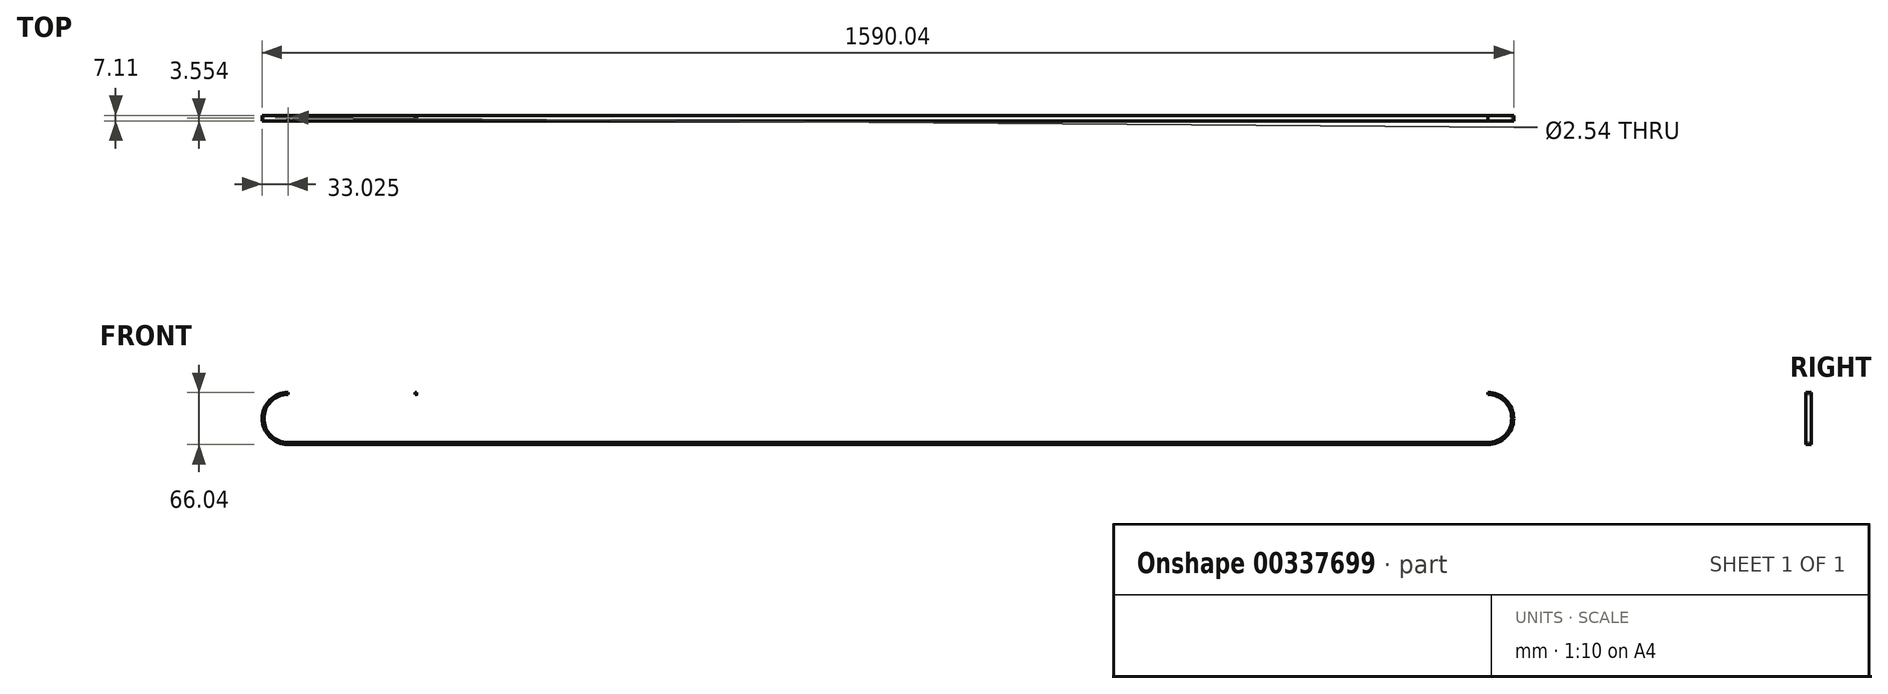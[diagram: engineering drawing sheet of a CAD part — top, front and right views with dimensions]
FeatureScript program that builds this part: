
annotation { "Feature Type Name" : "Feature", "Feature Type Description" : "" }
export const myFeature = defineFeature(function(context is Context, id is Id, definition is map)
    precondition{}
    {
        {
            var Q0;
            Q0=qCreatedBy(makeId("Front.planeOp"),FACE);
            var sketch = newSketch(context, id + "F0", { "sketchPlane" : qUnion([Q0])});
            skArc(sketch, "E0", {"start": v(1389.55, 13.92) * mm, "mid": v(1422.57, 46.94) * mm, "end": v(1389.55, 79.96) * mm});
            skArc(sketch, "E1", {"start": v(-134.45, 77.42) * mm, "mid": v(-164.93, 46.94) * mm, "end": v(-134.45, 16.46) * mm});
            skLineSegment(sketch, "E2", {"start": v(1389.55, 16.46) * mm, "end": v(-134.45, 16.46) * mm});
            skArc(sketch, "E3", {"start": v(-134.45, 79.96) * mm, "mid": v(-167.47, 46.94) * mm, "end": v(-134.45, 13.92) * mm});
            skLineSegment(sketch, "E4", {"start": v(-134.45, 13.92) * mm, "end": v(1389.55, 13.92) * mm});
            skLineSegment(sketch, "E5", {"start": v(-134.45, 79.96) * mm, "end": v(1389.55, 79.96) * mm});
            skLineSegment(sketch, "E6", {"start": v(-134.45, 77.42) * mm, "end": v(1389.55, 77.42) * mm});
            skArc(sketch, "E7", {"start": v(1389.55, 16.46) * mm, "mid": v(1420.03, 46.94) * mm, "end": v(1389.55, 77.42) * mm});
            skPoint(sketch, "E8", {"position": v(28.11, 79.96) * mm});
            skPoint(sketch, "E9", {"position": v(1330.37, 13.92) * mm});
            skSolve(sketch);
        }
        {
            var Q0;
            Q0 = qSketchRegion(id + "F0", true);
            extrude(context, id + "F1", {"entities" : qUnion([Q0]), "depth" : 7.11 * mm});
        }
        {
            var Q0;
            Q0=makeQuery(id+"F1.opExtrude","SWEPT_FACE",FACE,{"disambiguationData":[OSD([sQuery(id+"F0.wireOp",EDGE,"E5")])]});
            var sketch = newSketch(context, id + "F2", { "sketchPlane" : qUnion([Q0])});
            skLineSegment(sketch, "E10", {"start": v(28.11, 0) * mm, "end": v(28.11, -7.11) * mm});
            skPoint(sketch, "E11", {"position": v(28.11, -3.56) * mm});
            skCircle(sketch, "E12", {"center": v(28.11, -3.56) * mm, "radius": 1.08 * mm});
            skSolve(sketch);
        }
        {
            var Q0;
            {var subQ0=sQuery(id+"F2.wireOp",EDGE,"E12");var subQ1=sQuery(id+"F2.wireOp",EDGE,"E10");var subQ2=makeQuery(id+"F2.imprint","INTERSECT",VERTEX,{"disambiguationData":[OD(0.0)],"derivedFrom":[subQ1,subQ0]});Q0=makeQuery(id+"F2.imprint","IMPRINT",FACE,{"disambiguationData":[TD([[makeQuery(id+"F2.imprint","IMPRINT",EDGE,{"disambiguationData":[TD([[subQ2,-1.0]])],"derivedFrom":subQ1}),-1.0]])]});}
            var Q1;
            {var subQ0=sQuery(id+"F2.wireOp",EDGE,"E12");var subQ1=sQuery(id+"F2.wireOp",EDGE,"E10");var subQ2=makeQuery(id+"F2.imprint","INTERSECT",VERTEX,{"disambiguationData":[OD(0.0)],"derivedFrom":[subQ1,subQ0]});Q1=makeQuery(id+"F2.imprint","IMPRINT",FACE,{"disambiguationData":[TD([[makeQuery(id+"F2.imprint","IMPRINT",EDGE,{"disambiguationData":[TD([[subQ2,-1.0]])],"derivedFrom":subQ1}),1.0]])]});}
            extrude(context, id + "F3", {"entities" : qUnion([Q0, Q1]), "operationType" : NewBodyOperationType.REMOVE, "oppositeDirection" : true, "depth" : 25.4 * mm});
        }
        {
            var Q0;
            Q0=makeQuery(id+"F1.opExtrude","SWEPT_FACE",FACE,{"disambiguationData":[OSD([sQuery(id+"F0.wireOp",EDGE,"E4")])]});
            var sketch = newSketch(context, id + "F4", { "sketchPlane" : qUnion([Q0])});
            skSolve(sketch);
        }
        {
            var Q0;
            {var subQ0=sQuery(id+"F0.wireOp",EDGE,"E4");Q0=makeQuery(id+"F4.imprint","IMPRINT",FACE,{"disambiguationData":[TD([[makeQuery(id+"F4.imprint","IMPRINT",EDGE,{"derivedFrom":makeQuery(id+"F1.opExtrude","CAP_EDGE",EDGE,{"disambiguationData":[OSD([subQ0])],"isStart":true})}),1.0]])]});}
            var sketch = newSketch(context, id + "F5", { "sketchPlane" : qUnion([Q0])});
            skCircle(sketch, "E13", {"center": v(-134.45, 3.56) * mm, "radius": 1.27 * mm});
            skSolve(sketch);
        }
        {
            var Q0;
            {var subQ0=sQuery(id+"F5.wireOp",EDGE,"E13");var subQ1=makeQuery(id+"F4.imprint","IMPRINT",EDGE,{"derivedFrom":makeQuery(id+"F1.opExtrude","SWEPT_EDGE",EDGE,{"disambiguationData":[OSD([sQuery(id+"F0.wireOp",EDGE,"E3"),sQuery(id+"F0.wireOp",EDGE,"E4")])]})});var subQ2=makeQuery(id+"F5.imprint","INTERSECT",VERTEX,{"disambiguationData":[OD(0.0)],"derivedFrom":[subQ1,subQ0]});Q0=makeQuery(id+"F5.imprint","IMPRINT",FACE,{"disambiguationData":[TD([[makeQuery(id+"F5.imprint","IMPRINT",EDGE,{"disambiguationData":[TD([[subQ2,1.0]])],"derivedFrom":subQ0}),1.0]])]});}
            var Q1;
            {var subQ0=sQuery(id+"F5.wireOp",EDGE,"E13");var subQ1=makeQuery(id+"F4.imprint","IMPRINT",EDGE,{"derivedFrom":makeQuery(id+"F1.opExtrude","SWEPT_EDGE",EDGE,{"disambiguationData":[OSD([sQuery(id+"F0.wireOp",EDGE,"E3"),sQuery(id+"F0.wireOp",EDGE,"E4")])]})});var subQ2=makeQuery(id+"F5.imprint","INTERSECT",VERTEX,{"disambiguationData":[OD(0.0)],"derivedFrom":[subQ1,subQ0]});Q1=makeQuery(id+"F5.imprint","IMPRINT",FACE,{"disambiguationData":[TD([[makeQuery(id+"F5.imprint","IMPRINT",EDGE,{"disambiguationData":[TD([[subQ2,-1.0]])],"derivedFrom":subQ0}),1.0]])]});}
            var Q2;
            Q2=sQuery(id+"F5.wireOp",EDGE,"E13");
            extrude(context, id + "F6", {"entities" : qUnion([Q0, Q1]), "operationType" : NewBodyOperationType.REMOVE, "surfaceEntities" : qUnion([Q2]), "oppositeDirection" : true, "depth" : 25.4 * mm});
        }
    });
